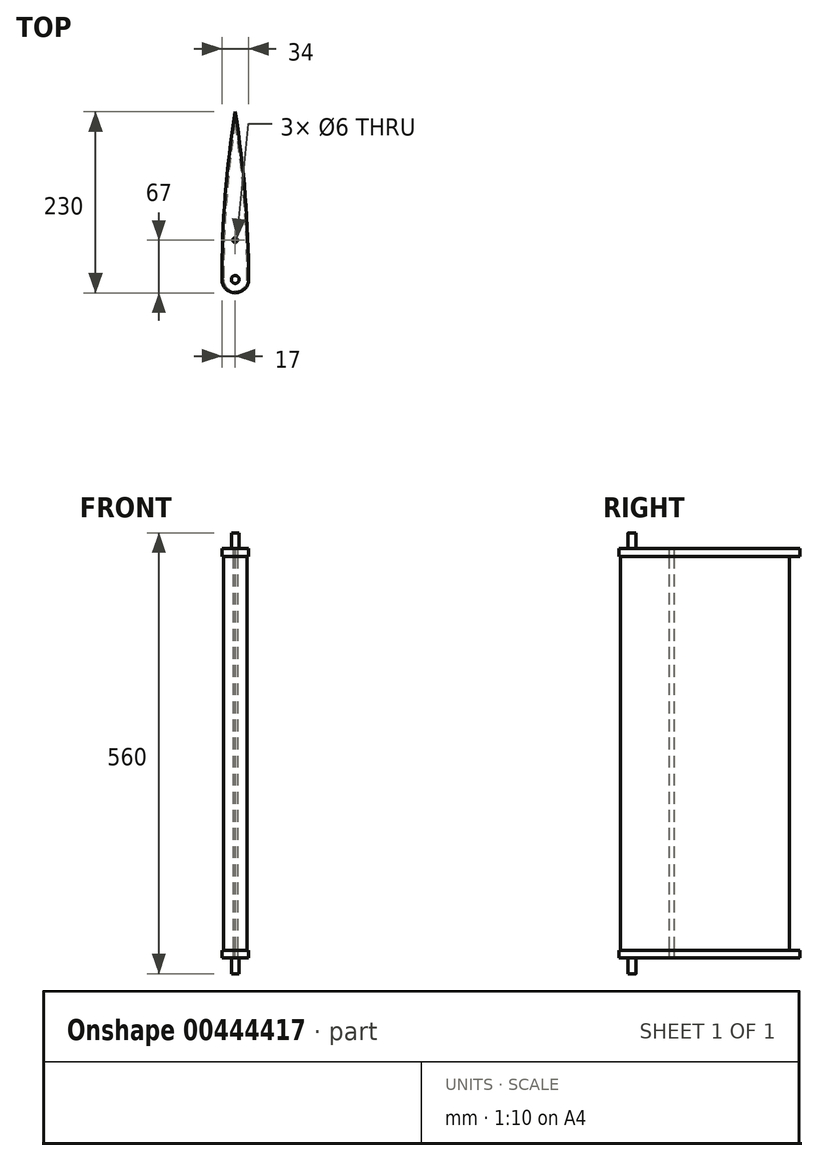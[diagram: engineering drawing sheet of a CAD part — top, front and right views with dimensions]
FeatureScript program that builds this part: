
annotation { "Feature Type Name" : "Feature", "Feature Type Description" : "" }
export const myFeature = defineFeature(function(context is Context, id is Id, definition is map)
    precondition{}
    {
        {
            var Q0;
            Q0=qCreatedBy(makeId("Top.planeOp"),FACE);
            var sketch = newSketch(context, id + "F0", { "sketchPlane" : qUnion([Q0])});
            skArc(sketch, "E0", {"start": v(-15, 0) * mm, "mid": v(0, -15) * mm, "end": v(15, 0) * mm});
            skArc(sketch, "E1", {"start": v(-15, 0) * mm, "mid": v(-11.24, 100.28) * mm, "end": v(0, 200) * mm});
            skLineSegment(sketch, "E2", {"start": v(0, 0) * mm, "end": v(0, 200) * mm, "construction": true});
            skArc(sketch, "E3.MirrorCS", {"start": v(15, 0) * mm, "mid": v(11.24, 100.28) * mm, "end": v(0, 200) * mm});
            skSolve(sketch);
        }
        {
            var Q0;
            Q0 = qSketchRegion(id + "F0", true);
            extrude(context, id + "F1", {"entities" : qUnion([Q0]), "endBound" : BoundingType.SYMMETRIC, "depth" : 500 * mm});
        }
        {
            var Q0;
            Q0=makeQuery(id+"F1.opExtrude","CAP_FACE",FACE,{"disambiguationData":[OSD([sQuery(id+"F0.wireOp",EDGE,"E0"),sQuery(id+"F0.wireOp",EDGE,"E1"),sQuery(id+"F0.wireOp",EDGE,"E3.MirrorCS")])],"isStart":false});
            var sketch = newSketch(context, id + "F2", { "sketchPlane" : qUnion([Q0])});
            skArc(sketch, "E4.0", {"start": v(-17, 0) * mm, "mid": v(0, -17) * mm, "end": v(17, 0) * mm});
            skArc(sketch, "E4.1", {"start": v(0, 213) * mm, "mid": v(-12.74, 106.84) * mm, "end": v(-17, 0) * mm});
            skArc(sketch, "E4.2", {"start": v(17, 0) * mm, "mid": v(12.74, 106.84) * mm, "end": v(0, 213) * mm});
            skSolve(sketch);
        }
        {
            var Q0;
            Q0 = qSketchRegion(id + "F2", true);
            extrude(context, id + "F3", {"entities" : qUnion([Q0]), "depth" : 10 * mm});
        }
        {
            var Q0;
            Q0=makeQuery(id+"F3.opExtrude","CAP_FACE",FACE,{"disambiguationData":[OSD([sQuery(id+"F2.wireOp",EDGE,"E4.0"),sQuery(id+"F2.wireOp",EDGE,"E4.1"),sQuery(id+"F2.wireOp",EDGE,"E4.2")])],"isStart":false});
            var sketch = newSketch(context, id + "F4", { "sketchPlane" : qUnion([Q0])});
            skCircle(sketch, "E5", {"center": v(0, 0) * mm, "radius": 5 * mm});
            skSolve(sketch);
        }
        {
            var Q0;
            Q0 = qSketchRegion(id + "F4", true);
            extrude(context, id + "F5", {"entities" : qUnion([Q0]), "operationType" : NewBodyOperationType.ADD, "depth" : 20 * mm});
        }
        {
            var Q0;
            Q0=makeQuery(id+"F3.opExtrude","SWEPT_BODY",BODY,{"disambiguationData":[OSD([sQuery(id+"F2.wireOp",EDGE,"E4.0"),sQuery(id+"F2.wireOp",EDGE,"E4.1"),sQuery(id+"F2.wireOp",EDGE,"E4.2")])]});
            var Q1;
            Q1=qCreatedBy(makeId("Top.planeOp"),FACE);
            mirror(context, id + "F6", {"entities" : qUnion([Q0]), "mirrorPlane" : qUnion([Q1])});
        }
        {
            var Q0;
            Q0=makeQuery(id+"F6.opPattern","COPY",FACE,{"derivedFrom":makeQuery(id+"F3.opExtrude","CAP_FACE",FACE,{"disambiguationData":[OSD([sQuery(id+"F2.wireOp",EDGE,"E4.0"),sQuery(id+"F2.wireOp",EDGE,"E4.1"),sQuery(id+"F2.wireOp",EDGE,"E4.2")])],"isStart":false}),"instanceName":"1"});
            var sketch = newSketch(context, id + "F7", { "sketchPlane" : qUnion([Q0])});
            skCircle(sketch, "E6", {"center": v(0, -50) * mm, "radius": 3 * mm});
            skLineSegment(sketch, "E7", {"start": v(0, 0) * mm, "end": v(0, -50) * mm, "construction": true});
            skSolve(sketch);
        }
        {
            var Q0;
            Q0 = qSketchRegion(id + "F7", true);
            extrude(context, id + "F8", {"entities" : qUnion([Q0]), "operationType" : NewBodyOperationType.REMOVE, "endBound" : BoundingType.THROUGH_ALL, "oppositeDirection" : true, "depth" : 25 * mm});
        }
    });
